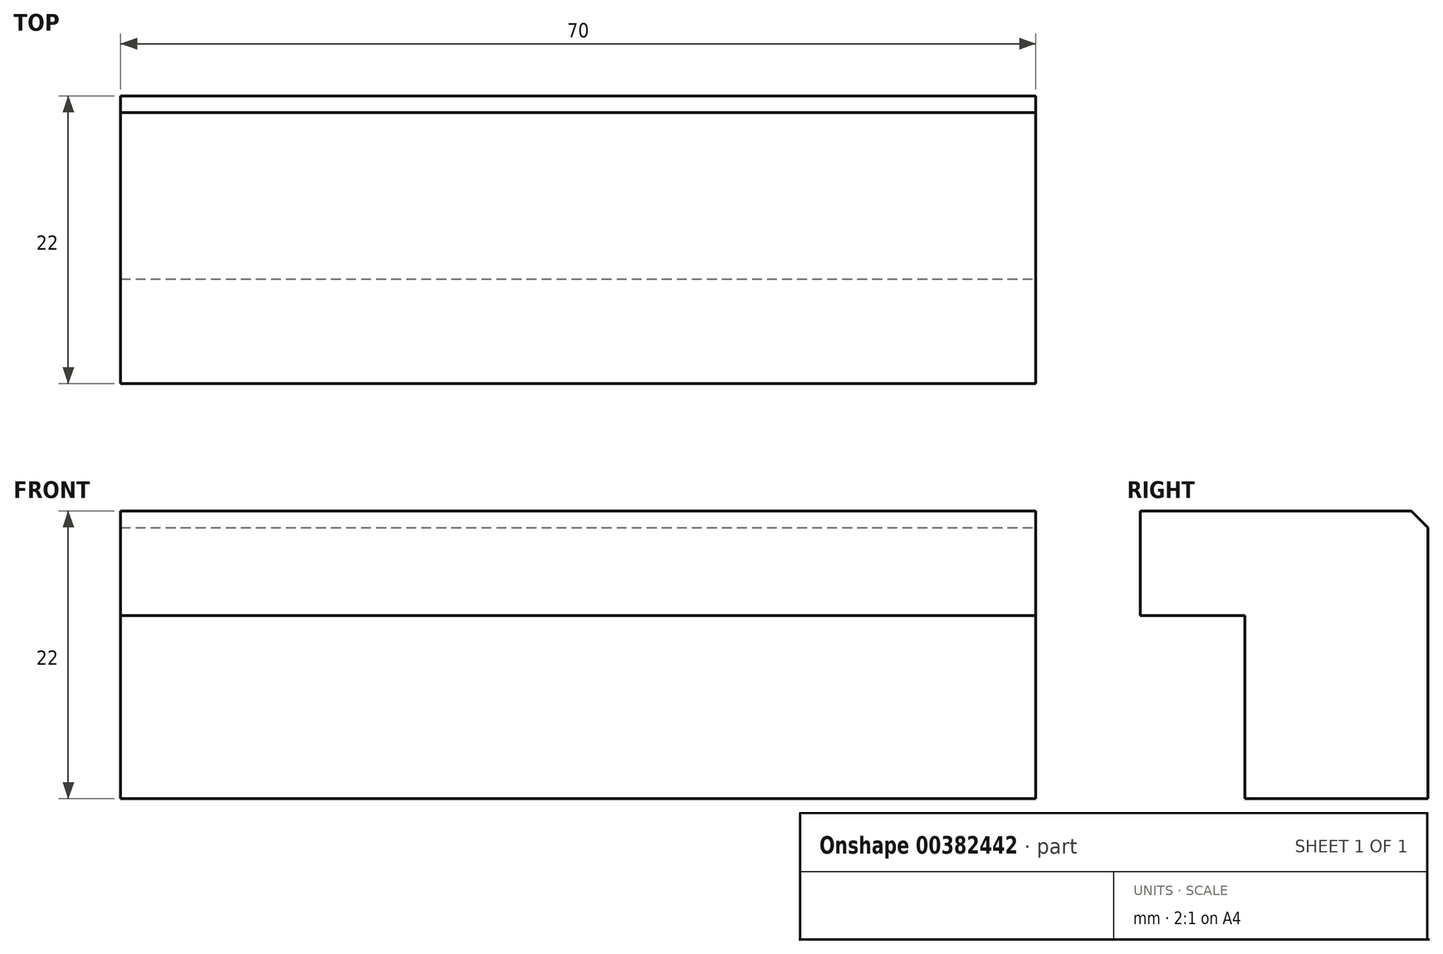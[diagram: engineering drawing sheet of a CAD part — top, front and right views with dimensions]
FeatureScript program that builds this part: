
annotation { "Feature Type Name" : "Feature", "Feature Type Description" : "" }
export const myFeature = defineFeature(function(context is Context, id is Id, definition is map)
    precondition{}
    {
        {
            var Q0;
            Q0=qCreatedBy(makeId("Front.planeOp"),FACE);
            var sketch = newSketch(context, id + "F0", { "sketchPlane" : qUnion([Q0])});
            skLineSegment(sketch, "E0.bottom", {"start": v(-35, 11) * mm, "end": v(35, 11) * mm});
            skLineSegment(sketch, "E0.top", {"start": v(-35, -11) * mm, "end": v(35, -11) * mm});
            skLineSegment(sketch, "E0.left", {"start": v(-35, 11) * mm, "end": v(-35, -11) * mm});
            skLineSegment(sketch, "E0.right", {"start": v(35, 11) * mm, "end": v(35, -11) * mm});
            skPoint(sketch, "E0.middle", {"position": v(0, 0) * mm});
            skLineSegment(sketch, "E1", {"start": v(-35, 3) * mm, "end": v(35, 3) * mm});
            skSolve(sketch);
        }
        {
            var Q0;
            {var subQ0=sQuery(id+"F0.wireOp",EDGE,"E0.bottom");Q0=makeQuery(id+"F0.imprint","IMPRINT",FACE,{"disambiguationData":[TD([[makeQuery(id+"F0.imprint","IMPRINT",EDGE,{"derivedFrom":subQ0}),-1.0]])]});}
            extrude(context, id + "F1", {"entities" : qUnion([Q0]), "depth" : 22 * mm});
        }
        {
            var Q0;
            {var subQ0=sQuery(id+"F0.wireOp",EDGE,"E0.top");Q0=makeQuery(id+"F0.imprint","IMPRINT",FACE,{"disambiguationData":[TD([[makeQuery(id+"F0.imprint","IMPRINT",EDGE,{"derivedFrom":subQ0}),1.0]])]});}
            extrude(context, id + "F2", {"entities" : qUnion([Q0]), "operationType" : NewBodyOperationType.ADD, "depth" : 14 * mm});
        }
        {
            var Q0;
            Q0=makeQuery(id+"F1.opExtrude","CAP_EDGE",EDGE,{"disambiguationData":[OSD([sQuery(id+"F0.wireOp",EDGE,"E0.bottom")])],"isStart":true});
            chamfer(context, id + "F3", {"entities" : qUnion([Q0]), "width" : 1.27 * mm, "tangentPropagation" : true});
        }
    });
